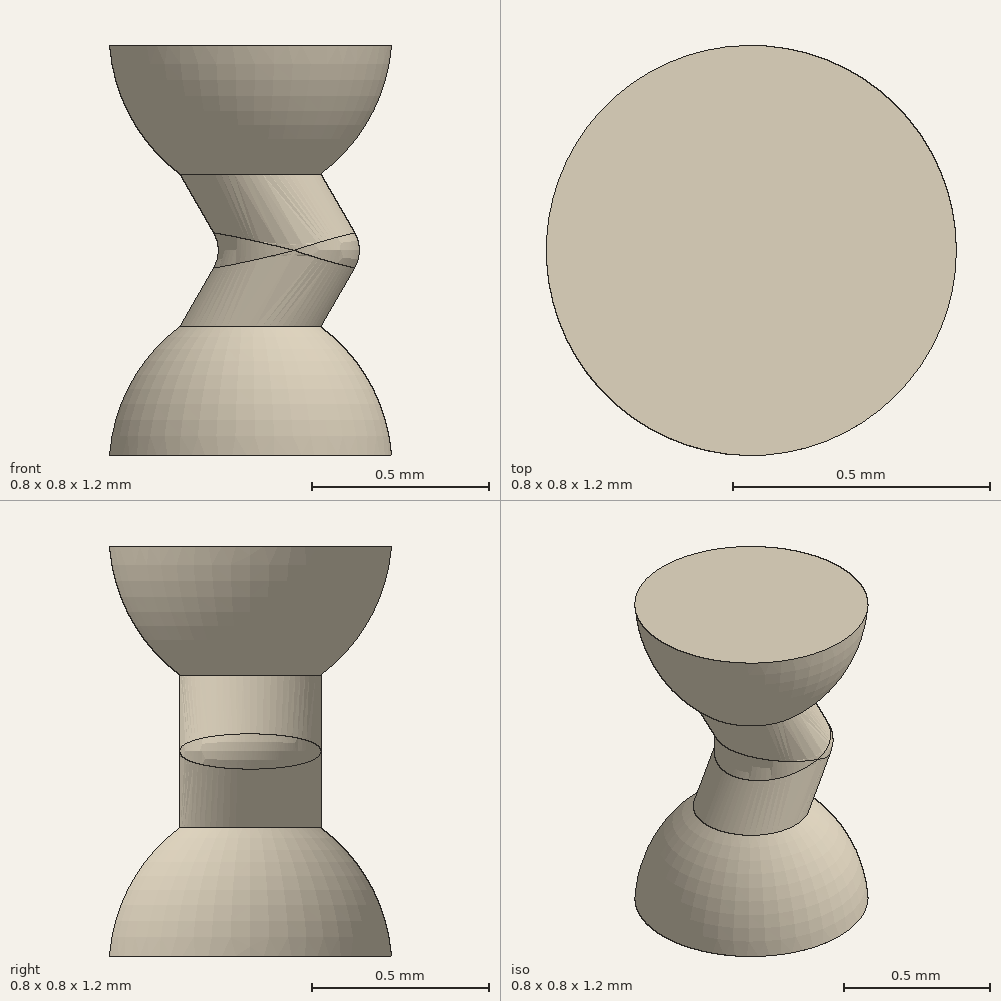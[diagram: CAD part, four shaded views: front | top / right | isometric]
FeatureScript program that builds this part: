
annotation { "Feature Type Name" : "Feature", "Feature Type Description" : "" }
export const myFeature = defineFeature(function(context is Context, id is Id, definition is map)
    precondition{}
    {
        {
            var Q0;
            Q0=qCreatedBy(makeId("Front.planeOp"),FACE);
            var sketch = newSketch(context, id + "F0", { "sketchPlane" : qUnion([Q0])});
            skLineSegment(sketch, "E0", {"start": v(0, 0) * mm, "end": v(-0.4, 0) * mm});
            skArc(sketch, "E1", {"start": v(-0.2, 0.36) * mm, "mid": v(-0.34, 0.2) * mm, "end": v(-0.4, 0) * mm});
            skPoint(sketch, "E1.startSnap0", {"position": v(-0.2, 0) * mm});
            skLineSegment(sketch, "E2", {"start": v(-0.2, 0.36) * mm, "end": v(0, 0.36) * mm});
            skLineSegment(sketch, "E3", {"start": v(0, 0.36) * mm, "end": v(0, 0) * mm});
            skLineSegment(sketch, "E4", {"start": v(0, 0.48) * mm, "end": v(0, -0.17) * mm, "construction": true});
            skSolve(sketch);
        }
        {
            var Q0;
            Q0=makeQuery(id+"F0.imprint","IMPRINT",FACE,{"disambiguationData":[TD([[makeQuery(id+"F0.imprint","IMPRINT",EDGE,{"derivedFrom":sQuery(id+"F0.wireOp",EDGE,"E0")}),-1.0]])]});
            var Q1;
            Q1=sQuery(id+"F0.wireOp",EDGE,"E4");
            revolve(context, id + "F1", {"surfaceOperationType" : NewSurfaceOperationType.NEW, "entities" : qUnion([Q0]), "axis" : qUnion([Q1]), "revolveType" : RevolveType.FULL});
        }
        {
            var Q0;
            Q0=qCreatedBy(makeId("Front.planeOp"),FACE);
            var sketch = newSketch(context, id + "F2", { "sketchPlane" : qUnion([Q0])});
            skLineSegment(sketch, "E5.0", {"start": v(-0.2, 0.36) * mm, "end": v(0.2, 0.36) * mm, "construction": true});
            skLineSegment(sketch, "E6", {"start": v(0, 0.36) * mm, "end": v(0.12, 0.58) * mm});
            skSolve(sketch);
        }
        {
            var Q0;
            Q0=makeQuery(id+"F1.opRevolve","SWEPT_FACE",FACE,{"disambiguationData":[OSD([sQuery(id+"F0.wireOp",EDGE,"E2")])]});
            var Q1;
            Q1=sQuery(id+"F2.wireOp",EDGE,"E6");
            sweep(context, id + "F3", {"operationType" : NewBodyOperationType.ADD, "profiles" : qUnion([Q0]), "path" : qUnion([Q1])});
        }
        {
            var Q0;
            Q0=makeQuery(id+"F1.opRevolve","SWEPT_BODY",BODY,{"disambiguationData":[OSD([sQuery(id+"F0.wireOp",EDGE,"E0"),sQuery(id+"F0.wireOp",EDGE,"E1"),sQuery(id+"F0.wireOp",EDGE,"E2"),sQuery(id+"F0.wireOp",EDGE,"E3")])]});
            var Q1;
            Q1=makeQuery(id+"F3.opSweep","CAP_FACE",FACE,{"disambiguationData":[OSD([sQuery(id+"F0.wireOp",EDGE,"E2"),sQuery(id+"F2.wireOp",VERTEX,"E6.end")])],"isStart":false});
            mirror(context, id + "F4", {"operationType" : NewBodyOperationType.ADD, "entities" : qUnion([Q0]), "mirrorPlane" : qUnion([Q1])});
        }
        {
            var Q0;
            {var subQ0=makeQuery(id+"F3.opSweep","CAP_EDGE",EDGE,{"disambiguationData":[OSD([sQuery(id+"F0.wireOp",EDGE,"E1"),sQuery(id+"F0.wireOp",EDGE,"E2"),sQuery(id+"F2.wireOp",VERTEX,"E6.end")])],"isStart":false});Q0=makeQuery(id+"F4.boolean.opBoolean","MERGE",EDGE,{"derivedFrom":[subQ0,makeQuery(id+"F4.opPattern","COPY",EDGE,{"derivedFrom":subQ0,"instanceName":"1"})]});}
            fillet(context, id + "F5", {"entities" : qUnion([Q0]), "radius" : 0.1 * mm, "tangentPropagation" : true, "allowEdgeOverflow" : false});
        }
    });
